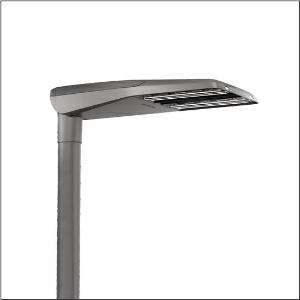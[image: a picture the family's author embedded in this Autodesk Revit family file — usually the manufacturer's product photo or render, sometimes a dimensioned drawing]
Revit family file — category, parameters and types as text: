
# Revit family: streetlight_sl_11_iq_midi___st1_0a_5xc3m51f08me_eb90
name_source: partatom
category: Lighting Fixtures
units: mm (PartAtom-declared; Revit-internal decimal feet)

## family parameters
Cut with Voids When Loaded = No
Host = Face
Light Source = No
Part Type = Normal
Room Calculation Point = No
Round Connector Dimension = Use Diameter
Shared = No

## types (1)
- --- (1 x LED, 17550 lm, 124.7 W, 3000K)
    Apparent Load = 125 VA
    CIE Flux Codes = 33 66 96 100 100
    Color Rendering = 70
    Color Temperature = 3000K
    Default Elevation = 1800 mm
    Description = Streetlight SL 11 iQ midi, mast luminaire, primary light control with 3 zone facetted reflector, of plastic, silver coated, highly specular, primary optical cover: cover, of PMMA, transparent, light distribution: ST1.0a, light emission: direct distribution, primary light characteristic: asymmetric, installation type: post-top, side-entry, LED, High Power LED, rated luminous flux: 17.550lm, luminous efficacy: 141lm/W, light colour: 730, colour temperature: 3000K, control: optimised constant luminous flux control (CLO 2.0), Street-Remote, Desk-Remote (wireless, voltage-free reading and setting of iQ features in the workshop via application-optimized NFC function/RFID function), Light-Fading, Smart-Wire, Night-Set, Lumen-Switch, Temp-Guard, Auto-Match, with cable H07RN-F 5x 1.5mm², mains connection: 230..240V, AC, 50/60Hz, connection cable pre-assembled, cable length: 12,5m, start of lifetime: 125W, end of service life: 132W, reduction: 57W, luminaire housing, of diecast aluminium, powder-coated, Siteco® metallic grey (DB 702S), please order mast flange separately, inclination adjustable without tools: 0°, 5°, 10°, 15° (post-top) | 0°, -5°, -10°, -15° (side-entry), sealing non-destructively replaceable, multi-level sealing system, length: 780mm, width: 376mm, height: 118mm, mast flange for spigot size: 42mm (side-entry): 5XC10008XM4, 60/48mm (side-entry/post-top): 5XC10108XM2, 76/60mm (side-entry/post-top): 5XC10108XM1, equipment: Power, protection rating (complete): IP66, insulation class (complete): insulation class II (safety insulation), certification: CE, ENEC, VDE, impact resistance: IK09, permissible operating ambient temperature for outdoor applications: -25..+50°C, standard-compliant lighting for roads and squares, Environmental Product Declaration (EPD) tested and certified by an independent institute, packaging unit: 1 piece

Light Distribution: ST1.0a
    Height = 118 mm
    Lamp = 1 x LED
    Lamp Light Flux = 17550 lm
    Lamp Power = 124.7 W
    Lamp count = 1
    Length = 780 mm
    Luminous efficacy = 141 lm/W
    Manufacturer = Siteco
    ModVariant = No
    Model = 5XC3M51F08ME
    Number of Poles = 1
    OnlyDefault = Yes
    Power Factor = 1
    Product Name = Streetlight SL 11 iQ midi | ST1.0a
    Product group = mast luminaire | pylon top
    ProductGroupID = 6100
    Protection Class = Protection class II
    Protection Degree = IP 66
    RLX_Detail_Level = 1
    RLX_Emergency_Light_Flux = 0 lm
    RLX_Emergency_Type = 0
    RLX_Emergency_Type_DB = No
    RlxData = <blob elided: 70197 chars, md5=89798681>
    Socket = socket
    Standby Power = 0 W
    System Light Flux = 17550 lm
    System Power = 125 W
    Type Comments = factory setting: luminous flux: 100 % | dim-lin: 254 | 557 mA
    Type Image = l_1005960.jpg
    URL = http://relux.com
    VarID = @adj_020777
    Voltage = 0 V
    Weight = 0.00 kg
    Width = 376 mm

## geometry (parser evidence)
native form markers: Blend x4, Sweep x10
no freeform markers — native parametric forms only
